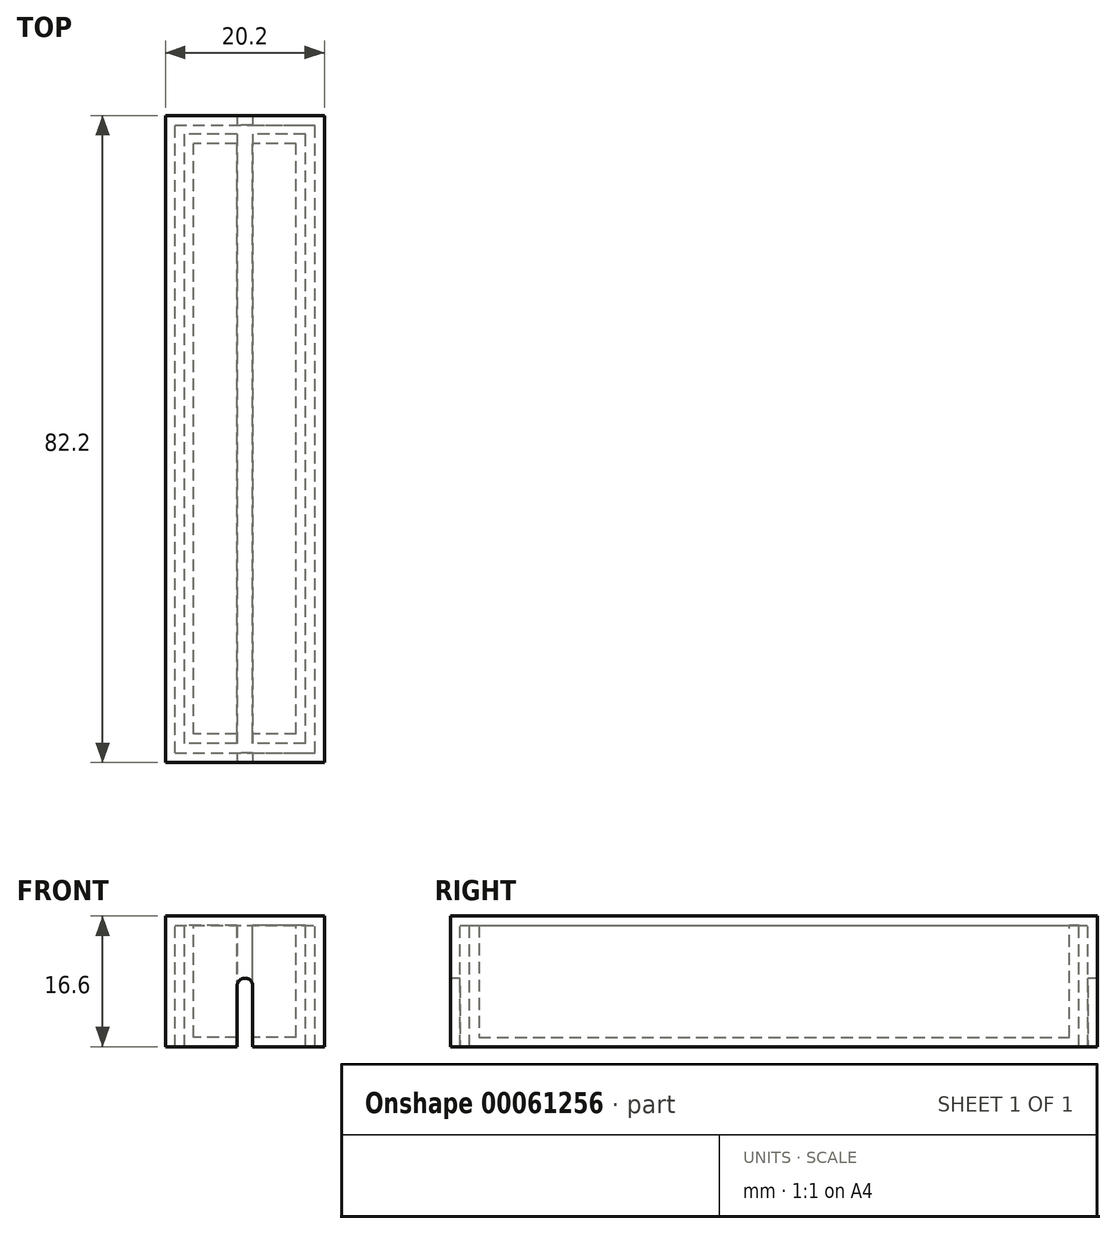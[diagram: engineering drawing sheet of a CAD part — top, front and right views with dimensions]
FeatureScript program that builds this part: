
annotation { "Feature Type Name" : "Feature", "Feature Type Description" : "" }
export const myFeature = defineFeature(function(context is Context, id is Id, definition is map)
    precondition{}
    {
        {
            assignVariable(context, id + "F0", {"name" : "length", "anyValue" : 75});
        }
        {
            var Q0;
            Q0=qCreatedBy(makeId("Front.planeOp"),FACE);
            var sketch = newSketch(context, id + "F1", { "sketchPlane" : qUnion([Q0])});
            skLineSegment(sketch, "E0.rect.bottom", {"start": v(6.5, -6.5) * mm, "end": v(-6.5, -6.5) * mm});
            skLineSegment(sketch, "E0.rect.top", {"start": v(6.5, 6.5) * mm, "end": v(1, 6.5) * mm});
            skLineSegment(sketch, "E0.rect.left", {"start": v(6.5, -6.5) * mm, "end": v(6.5, 6.5) * mm});
            skLineSegment(sketch, "E0.rect.right", {"start": v(-6.5, -6.5) * mm, "end": v(-6.5, 6.5) * mm});
            skPoint(sketch, "E0.rect.middle", {"position": v(0, 0) * mm});
            skLineSegment(sketch, "E1.0", {"start": v(-7.7, -7.7) * mm, "end": v(-7.7, 7.7) * mm});
            skLineSegment(sketch, "E1.1", {"start": v(7.7, -7.7) * mm, "end": v(-7.7, -7.7) * mm});
            skLineSegment(sketch, "E1.2", {"start": v(7.7, -7.7) * mm, "end": v(7.7, 7.7) * mm});
            skLineSegment(sketch, "E1.3", {"start": v(7.7, 7.7) * mm, "end": v(-7.7, 7.7) * mm});
            skArc(sketch, "E2", {"start": v(-1, 0) * mm, "mid": v(0, -1) * mm, "end": v(1, 0) * mm});
            skLineSegment(sketch, "E3", {"start": v(-1, 0) * mm, "end": v(-1, 6.5) * mm});
            skPoint(sketch, "E3.endSnap0", {"position": v(0, 6.5) * mm});
            skLineSegment(sketch, "E4", {"start": v(1, 0) * mm, "end": v(1, 6.5) * mm});
            skLineSegment(sketch, "E5.trimOffspring", {"start": v(-1, 6.5) * mm, "end": v(-6.5, 6.5) * mm});
            skLineSegment(sketch, "E6", {"start": v(1, 6.5) * mm, "end": v(1, 7.7) * mm});
            skLineSegment(sketch, "E7", {"start": v(-1, 6.5) * mm, "end": v(-1, 7.7) * mm});
            skPoint(sketch, "E7.endSnap0", {"position": v(0, 7.7) * mm});
            skLineSegment(sketch, "E8", {"start": v(-6.5, 6.5) * mm, "end": v(-6.5, 7.7) * mm});
            skLineSegment(sketch, "E9", {"start": v(6.5, 6.5) * mm, "end": v(6.5, 7.7) * mm});
            skSolve(sketch);
        }
        {
            var Q0;
            Q0=makeQuery(id+"F1.imprint","IMPRINT",FACE,{"disambiguationData":[TD([[makeQuery(id+"F1.imprint","IMPRINT",EDGE,{"derivedFrom":sQuery(id+"F1.wireOp",EDGE,"E0.rect.bottom")}),1.0]])]});
            extrude(context, id + "F2", {"entities" : qUnion([Q0]), "depth" : getVariable(context, 'length') * mm});
        }
        {
            var Q0;
            Q0=makeQuery(id+"F1.imprint","IMPRINT",FACE,{"disambiguationData":[TD([[makeQuery(id+"F1.imprint","IMPRINT",EDGE,{"derivedFrom":sQuery(id+"F1.wireOp",EDGE,"E5.trimOffspring")}),-1.0]])]});
            var Q1;
            Q1=makeQuery(id+"F1.imprint","IMPRINT",FACE,{"disambiguationData":[TD([[makeQuery(id+"F1.imprint","IMPRINT",EDGE,{"derivedFrom":sQuery(id+"F1.wireOp",EDGE,"E0.rect.bottom")}),-1.0]])]});
            var Q2;
            Q2=makeQuery(id+"F1.imprint","IMPRINT",FACE,{"disambiguationData":[TD([[makeQuery(id+"F1.imprint","IMPRINT",EDGE,{"derivedFrom":sQuery(id+"F1.wireOp",EDGE,"E0.rect.bottom")}),1.0]])]});
            var Q3;
            Q3=makeQuery(id+"F1.imprint","IMPRINT",FACE,{"disambiguationData":[TD([[makeQuery(id+"F1.imprint","IMPRINT",EDGE,{"derivedFrom":sQuery(id+"F1.wireOp",EDGE,"E0.rect.top")}),-1.0]])]});
            extrude(context, id + "F3", {"entities" : qUnion([Q0, Q1, Q2, Q3]), "operationType" : NewBodyOperationType.ADD, "oppositeDirection" : true, "depth" : 1.2 * mm});
        }
        {
            var Q0;
            Q0=makeQuery(id+"F2.opExtrude","CAP_FACE",FACE,{"disambiguationData":[OSD([sQuery(id+"F1.wireOp",EDGE,"E0.rect.bottom"),sQuery(id+"F1.wireOp",EDGE,"E0.rect.left"),sQuery(id+"F1.wireOp",EDGE,"E0.rect.right"),sQuery(id+"F1.wireOp",EDGE,"E1.0"),sQuery(id+"F1.wireOp",EDGE,"E1.1"),sQuery(id+"F1.wireOp",EDGE,"E1.2"),sQuery(id+"F1.wireOp",EDGE,"E1.3"),sQuery(id+"F1.wireOp",EDGE,"E8"),sQuery(id+"F1.wireOp",EDGE,"E9")])],"isStart":false});
            var sketch = newSketch(context, id + "F4", { "sketchPlane" : qUnion([Q0])});
            skLineSegment(sketch, "E10.0.0", {"start": v(-6.5, -6.5) * mm, "end": v(6.5, -6.5) * mm});
            skLineSegment(sketch, "E10.0.1", {"start": v(6.5, -6.5) * mm, "end": v(6.5, 6.5) * mm});
            skLineSegment(sketch, "E10.0.2", {"start": v(6.5, 6.5) * mm, "end": v(1, 6.5) * mm});
            skLineSegment(sketch, "E10.0.3", {"start": v(1, 6.5) * mm, "end": v(1, 0) * mm});
            skArc(sketch, "E10.0.4", {"start": v(1, 0) * mm, "mid": v(0, -1) * mm, "end": v(-1, 0) * mm});
            skLineSegment(sketch, "E10.0.5", {"start": v(-1, 0) * mm, "end": v(-1, 6.5) * mm});
            skLineSegment(sketch, "E10.0.6", {"start": v(-1, 6.5) * mm, "end": v(-6.5, 6.5) * mm});
            skLineSegment(sketch, "E10.0.7", {"start": v(-6.5, 6.5) * mm, "end": v(-6.5, -6.5) * mm});
            skLineSegment(sketch, "E11.0", {"start": v(7.7, 7.7) * mm, "end": v(-7.7, 7.7) * mm});
            skLineSegment(sketch, "E12.0", {"start": v(7.7, -7.7) * mm, "end": v(7.7, 7.7) * mm});
            skLineSegment(sketch, "E13.0", {"start": v(7.7, -7.7) * mm, "end": v(-7.7, -7.7) * mm});
            skLineSegment(sketch, "E14.0", {"start": v(-7.7, -7.7) * mm, "end": v(-7.7, 7.7) * mm});
            skLineSegment(sketch, "E15.0", {"start": v(1, 6.5) * mm, "end": v(1, 7.7) * mm});
            skLineSegment(sketch, "E15.1", {"start": v(-1, 6.5) * mm, "end": v(-1, 7.7) * mm});
            skSolve(sketch);
        }
        {
            var Q0;
            Q0=makeQuery(id+"F4.imprint","IMPRINT",FACE,{"disambiguationData":[TD([[makeQuery(id+"F4.imprint","IMPRINT",EDGE,{"derivedFrom":sQuery(id+"F4.wireOp",EDGE,"E10.0.0")}),-1.0]])]});
            var Q1;
            Q1=makeQuery(id+"F4.imprint","IMPRINT",FACE,{"disambiguationData":[TD([[makeQuery(id+"F4.imprint","IMPRINT",EDGE,{"derivedFrom":sQuery(id+"F4.wireOp",EDGE,"E10.0.0")}),1.0]])]});
            var Q2;
            {var subQ0=sQuery(id+"F4.wireOp",EDGE,"E10.0.2");Q2=makeQuery(id+"F4.imprint","IMPRINT",FACE,{"disambiguationData":[TD([[makeQuery(id+"F4.imprint","IMPRINT",EDGE,{"derivedFrom":subQ0}),-1.0]])]});}
            var Q3;
            {var subQ0=sQuery(id+"F4.wireOp",EDGE,"E10.0.6");Q3=makeQuery(id+"F4.imprint","IMPRINT",FACE,{"disambiguationData":[TD([[makeQuery(id+"F4.imprint","IMPRINT",EDGE,{"derivedFrom":subQ0}),-1.0]])]});}
            extrude(context, id + "F5", {"entities" : qUnion([Q0, Q1, Q2, Q3]), "operationType" : NewBodyOperationType.ADD, "depth" : 1.2 * mm});
        }
        {
            var Q0;
            {var subQ0=sQuery(id+"F4.wireOp",EDGE,"E11.0");var subQ3=sQuery(id+"F1.wireOp",EDGE,"E1.3");var subQ5=makeQuery(id+"F1.imprint","IMPRINT",EDGE,{"disambiguationData":[TD([[makeQuery(id+"F1.imprint","INTERSECT",VERTEX,{"derivedFrom":[sQuery(id+"F1.wireOp",EDGE,"E1.0"),subQ3]}),1.0]])],"derivedFrom":subQ3});Q0=makeQuery(id+"F5.boolean.opBoolean","MERGE",FACE,{"derivedFrom":[makeQuery(id+"F3.boolean.opBoolean","MERGE",FACE,{"derivedFrom":[makeQuery(id+"F2.opExtrude","SWEPT_FACE",FACE,{"disambiguationData":[OSD([subQ3]),TDD([subQ5])]}),makeQuery(id+"F3.opExtrude","SWEPT_FACE",FACE,{"disambiguationData":[OSD([subQ3]),TDD([makeQuery(id+"F1.imprint","IMPRINT",EDGE,{"disambiguationData":[TD([[makeQuery(id+"F1.imprint","INTERSECT",VERTEX,{"derivedFrom":[subQ3,sQuery(id+"F1.wireOp",EDGE,"E7")]}),-1.0]])],"derivedFrom":subQ3}),subQ5])]})]}),makeQuery(id+"F5.opExtrude","SWEPT_FACE",FACE,{"disambiguationData":[OSD([subQ0]),TDD([makeQuery(id+"F4.imprint","IMPRINT",EDGE,{"disambiguationData":[TD([[makeQuery(id+"F4.imprint","INTERSECT",VERTEX,{"derivedFrom":[subQ0,sQuery(id+"F4.wireOp",EDGE,"E15.1")]}),-1.0]])],"derivedFrom":subQ0}),makeQuery(id+"F4.imprint","IMPRINT",EDGE,{"disambiguationData":[TD([[makeQuery(id+"F4.imprint","INTERSECT",VERTEX,{"derivedFrom":[subQ0,sQuery(id+"F4.wireOp",EDGE,"E14.0")]}),1.0]])],"derivedFrom":subQ0})])]})]});}
            var sketch = newSketch(context, id + "F6", { "sketchPlane" : qUnion([Q0])});
            skLineSegment(sketch, "E16.0.0", {"start": v(7.7, -76.2) * mm, "end": v(7.7, 1.2) * mm});
            skLineSegment(sketch, "E17.0", {"start": v(-7.7, -76.2) * mm, "end": v(-7.7, 1.2) * mm});
            skLineSegment(sketch, "E18", {"start": v(-7.7, -76.2) * mm, "end": v(7.7, -76.2) * mm});
            skLineSegment(sketch, "E19", {"start": v(-7.7, 1.2) * mm, "end": v(7.7, 1.2) * mm});
            skLineSegment(sketch, "E20.0", {"start": v(-8.9, -77.4) * mm, "end": v(-8.9, 2.4) * mm});
            skLineSegment(sketch, "E20.1", {"start": v(-8.9, -77.4) * mm, "end": v(8.9, -77.4) * mm});
            skLineSegment(sketch, "E20.2", {"start": v(8.9, -77.4) * mm, "end": v(8.9, 2.4) * mm});
            skLineSegment(sketch, "E20.3", {"start": v(-8.9, 2.4) * mm, "end": v(8.9, 2.4) * mm});
            skLineSegment(sketch, "E21.0", {"start": v(-10.1, -78.6) * mm, "end": v(-10.1, 3.6) * mm});
            skLineSegment(sketch, "E21.1", {"start": v(-10.1, -78.6) * mm, "end": v(10.1, -78.6) * mm});
            skLineSegment(sketch, "E21.2", {"start": v(10.1, -78.6) * mm, "end": v(10.1, 3.6) * mm});
            skLineSegment(sketch, "E21.3", {"start": v(-10.1, 3.6) * mm, "end": v(10.1, 3.6) * mm});
            skSolve(sketch);
        }
        {
            var Q0;
            Q0=makeQuery(id+"F6.imprint","IMPRINT",FACE,{"disambiguationData":[TD([[makeQuery(id+"F6.imprint","IMPRINT",EDGE,{"derivedFrom":sQuery(id+"F6.wireOp",EDGE,"E20.0")}),1.0]])]});
            var Q1;
            {var subQ0=sQuery(id+"F1.wireOp",EDGE,"E1.1");Q1=makeQuery(id+"F5.boolean.opBoolean","MERGE",FACE,{"derivedFrom":[makeQuery(id+"F3.boolean.opBoolean","MERGE",FACE,{"derivedFrom":[makeQuery(id+"F2.opExtrude","SWEPT_FACE",FACE,{"disambiguationData":[OSD([subQ0])]}),makeQuery(id+"F3.opExtrude","SWEPT_FACE",FACE,{"disambiguationData":[OSD([subQ0])]})]}),makeQuery(id+"F5.opExtrude","SWEPT_FACE",FACE,{"disambiguationData":[OSD([sQuery(id+"F4.wireOp",EDGE,"E13.0")])]})]});}
            var Q2;
            Q2=makeQuery(id+"F2.opExtrude","SWEPT_BODY",BODY,{"disambiguationData":[OSD([sQuery(id+"F1.wireOp",EDGE,"E0.rect.bottom"),sQuery(id+"F1.wireOp",EDGE,"E0.rect.left"),sQuery(id+"F1.wireOp",EDGE,"E0.rect.right"),sQuery(id+"F1.wireOp",EDGE,"E1.0"),sQuery(id+"F1.wireOp",EDGE,"E1.1"),sQuery(id+"F1.wireOp",EDGE,"E1.2"),sQuery(id+"F1.wireOp",EDGE,"E1.3"),sQuery(id+"F1.wireOp",EDGE,"E8"),sQuery(id+"F1.wireOp",EDGE,"E9")])]});
            extrude(context, id + "F7", {"entities" : qUnion([Q0]), "endBound" : BoundingType.UP_TO_SURFACE, "oppositeDirection" : true, "endBoundEntityFace" : qUnion([Q1]), "endBoundEntityBody" : qUnion([Q2]), "depth" : 25 * mm});
        }
        {
            var Q0;
            Q0=makeQuery(id+"F7.opExtrude","SWEPT_FACE",FACE,{"disambiguationData":[OSD([sQuery(id+"F6.wireOp",EDGE,"E21.1")])]});
            var sketch = newSketch(context, id + "F8", { "sketchPlane" : qUnion([Q0])});
            skArc(sketch, "E22", {"start": v(1, 0) * mm, "mid": v(0, 1) * mm, "end": v(-1, 0) * mm});
            skLineSegment(sketch, "E23", {"start": v(-1, 0) * mm, "end": v(-1, -7.7) * mm});
            skPoint(sketch, "E23.endSnap0", {"position": v(0, -7.7) * mm});
            skLineSegment(sketch, "E24", {"start": v(1, 0) * mm, "end": v(1, -7.7) * mm});
            skLineSegment(sketch, "E25.0", {"start": v(-1, -7.7) * mm, "end": v(1, -7.7) * mm});
            skPoint(sketch, "E26.orphan", {"position": v(10.1, -7.7) * mm});
            skPoint(sketch, "E27.orphan", {"position": v(-10.1, -7.7) * mm});
            skSolve(sketch);
        }
        {
            var Q0;
            Q0=makeQuery(id+"F8.imprint","IMPRINT",FACE,{"disambiguationData":[TD([[makeQuery(id+"F8.imprint","IMPRINT",EDGE,{"derivedFrom":sQuery(id+"F8.wireOp",EDGE,"E22")}),1.0]])]});
            extrude(context, id + "F9", {"entities" : qUnion([Q0]), "operationType" : NewBodyOperationType.REMOVE, "endBound" : BoundingType.THROUGH_ALL, "oppositeDirection" : true, "depth" : 25 * mm});
        }
        {
            var Q0;
            Q0=makeQuery(id+"F7.opExtrude","CAP_FACE",FACE,{"disambiguationData":[OSD([sQuery(id+"F6.wireOp",EDGE,"E20.0"),sQuery(id+"F6.wireOp",EDGE,"E20.1"),sQuery(id+"F6.wireOp",EDGE,"E20.2"),sQuery(id+"F6.wireOp",EDGE,"E20.3"),sQuery(id+"F6.wireOp",EDGE,"E21.0"),sQuery(id+"F6.wireOp",EDGE,"E21.1"),sQuery(id+"F6.wireOp",EDGE,"E21.2"),sQuery(id+"F6.wireOp",EDGE,"E21.3")])],"isStart":true});
            var sketch = newSketch(context, id + "F10", { "sketchPlane" : qUnion([Q0])});
            skLineSegment(sketch, "E28.bottom", {"start": v(10.1, 3.6) * mm, "end": v(-10.1, 3.6) * mm});
            skLineSegment(sketch, "E28.top", {"start": v(10.1, -78.6) * mm, "end": v(-10.1, -78.6) * mm});
            skLineSegment(sketch, "E28.left", {"start": v(10.1, 3.6) * mm, "end": v(10.1, -78.6) * mm});
            skLineSegment(sketch, "E28.right", {"start": v(-10.1, 3.6) * mm, "end": v(-10.1, -78.6) * mm});
            skSolve(sketch);
        }
        {
            var Q0;
            Q0 = qSketchRegion(id + "F10", true);
            extrude(context, id + "F11", {"entities" : qUnion([Q0]), "operationType" : NewBodyOperationType.ADD, "depth" : 1.2 * mm});
        }
    });
